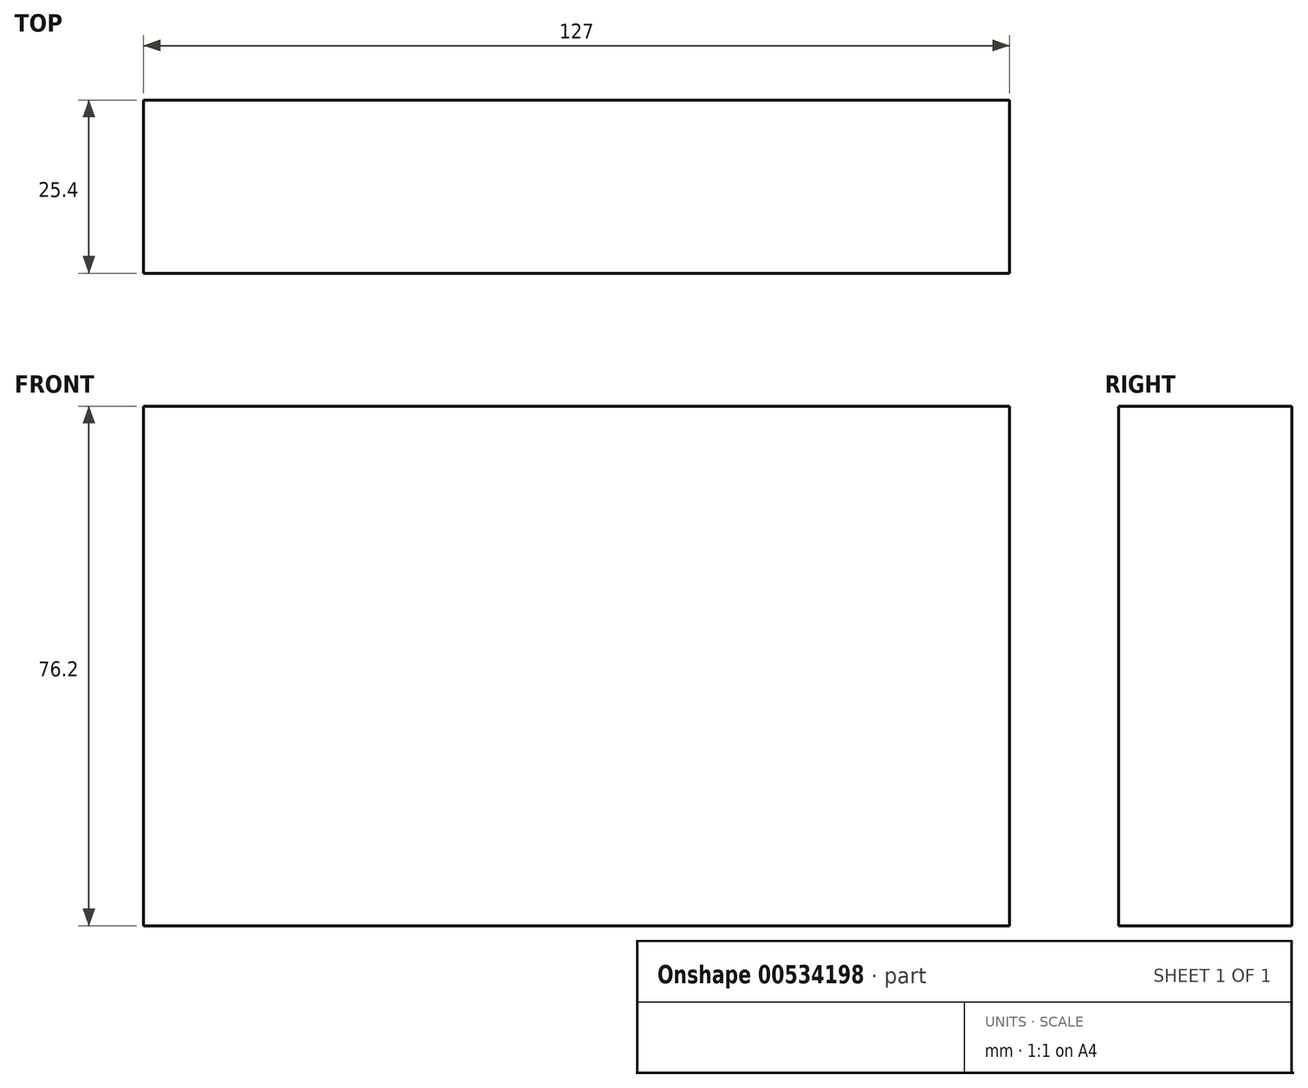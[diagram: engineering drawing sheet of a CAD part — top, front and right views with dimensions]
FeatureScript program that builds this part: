
annotation { "Feature Type Name" : "Feature", "Feature Type Description" : "" }
export const myFeature = defineFeature(function(context is Context, id is Id, definition is map)
    precondition{}
    {
        {
            var Q0;
            Q0=qCreatedBy(makeId("Front.planeOp"),FACE);
            var sketch = newSketch(context, id + "F0", { "sketchPlane" : qUnion([Q0])});
            skLineSegment(sketch, "E0.bottom", {"start": v(63.5, 38.1) * mm, "end": v(-63.5, 38.1) * mm});
            skLineSegment(sketch, "E0.top", {"start": v(63.5, -38.1) * mm, "end": v(-63.5, -38.1) * mm});
            skLineSegment(sketch, "E0.left", {"start": v(63.5, 38.1) * mm, "end": v(63.5, -38.1) * mm});
            skLineSegment(sketch, "E0.right", {"start": v(-63.5, 38.1) * mm, "end": v(-63.5, -38.1) * mm});
            skPoint(sketch, "E0.middle", {"position": v(0, 0) * mm});
            skSolve(sketch);
        }
        {
            var Q0;
            Q0=makeQuery(id+"F0.imprint","IMPRINT",FACE,{"disambiguationData":[TD([[makeQuery(id+"F0.imprint","IMPRINT",EDGE,{"derivedFrom":sQuery(id+"F0.wireOp",EDGE,"E0.bottom")}),1.0]])]});
            extrude(context, id + "F1", {"entities" : qUnion([Q0]), "endBound" : BoundingType.SYMMETRIC, "depth" : 25.4 * mm, "offsetDistance" : 25.4 * mm});
        }
    });
